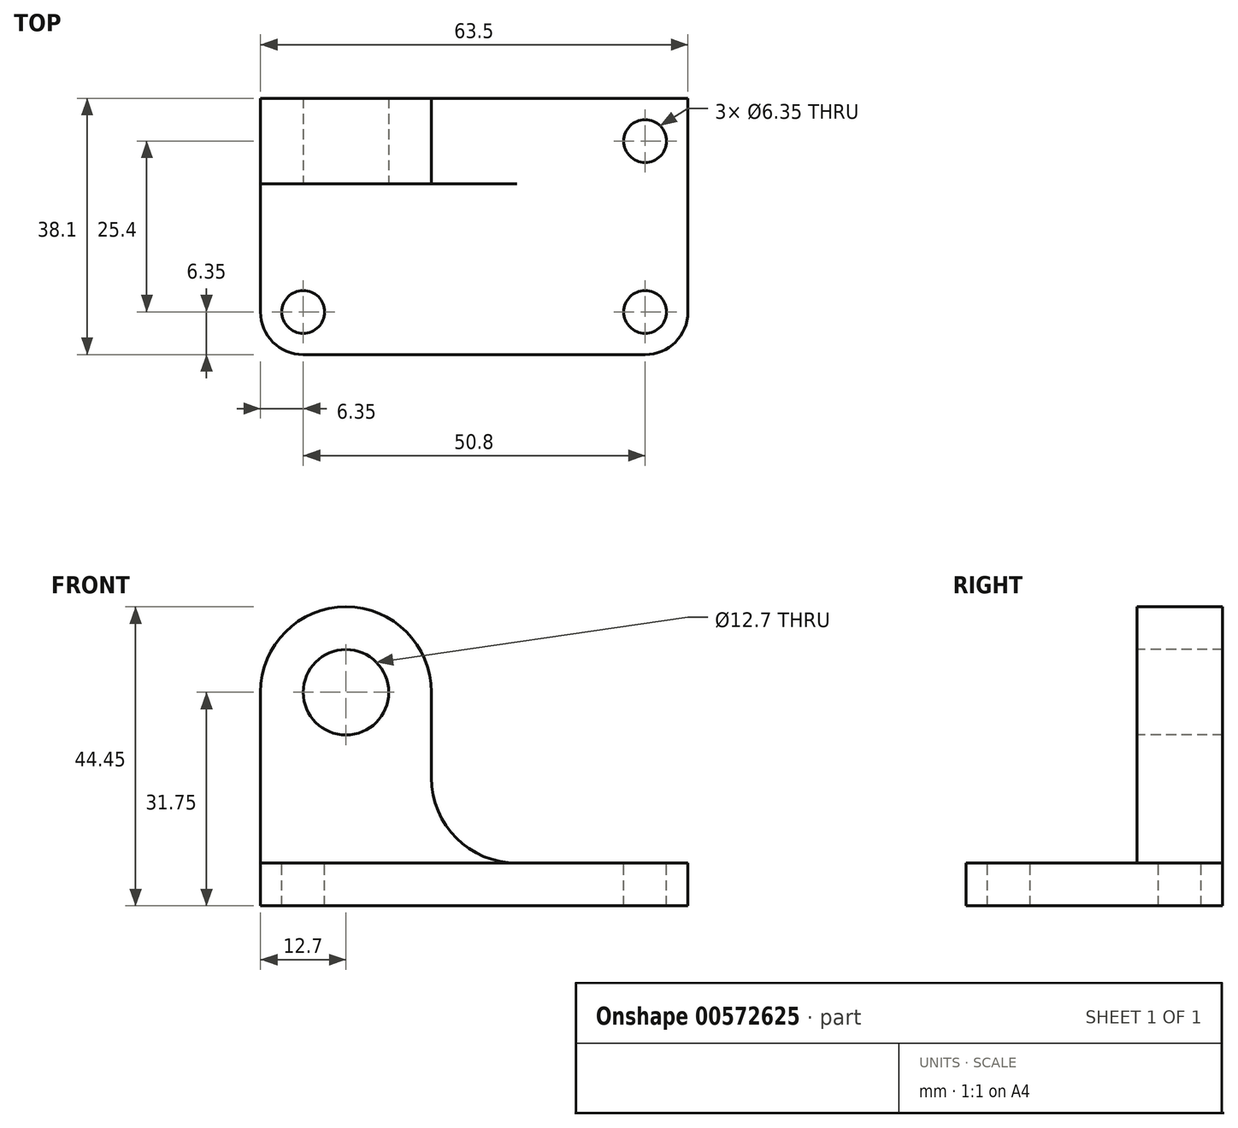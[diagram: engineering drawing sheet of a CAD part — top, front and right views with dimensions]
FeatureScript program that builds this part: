
annotation { "Feature Type Name" : "Feature", "Feature Type Description" : "" }
export const myFeature = defineFeature(function(context is Context, id is Id, definition is map)
    precondition{}
    {
        {
            var Q0;
            Q0=qCreatedBy(makeId("Front.planeOp"),FACE);
            var sketch = newSketch(context, id + "F0", { "sketchPlane" : qUnion([Q0])});
            skLineSegment(sketch, "E0", {"start": v(0, 0) * mm, "end": v(63.5, 0) * mm});
            skLineSegment(sketch, "E1", {"start": v(63.5, 0) * mm, "end": v(63.5, 6.35) * mm});
            skLineSegment(sketch, "E2", {"start": v(63.5, 6.35) * mm, "end": v(38.1, 6.35) * mm});
            skLineSegment(sketch, "E3", {"start": v(38.1, 6.35) * mm, "end": v(38.1, 44.45) * mm});
            skLineSegment(sketch, "E4", {"start": v(38.1, 44.45) * mm, "end": v(0, 44.45) * mm});
            skLineSegment(sketch, "E5", {"start": v(0, 44.45) * mm, "end": v(0, 0) * mm});
            skSolve(sketch);
        }
        {
            var Q0;
            Q0 = qSketchRegion(id + "F0", true);
            extrude(context, id + "F1", {"entities" : qUnion([Q0]), "depth" : 38.1 * mm, "offsetDistance" : 25.4 * mm});
        }
        {
            var Q0;
            Q0=makeQuery(id+"F1.opExtrude","SWEPT_FACE",FACE,{"disambiguationData":[OSD([sQuery(id+"F0.wireOp",EDGE,"E3")])]});
            var sketch = newSketch(context, id + "F2", { "sketchPlane" : qUnion([Q0])});
            skLineSegment(sketch, "E6", {"start": v(-38.1, 6.35) * mm, "end": v(-12.7, 6.35) * mm});
            skLineSegment(sketch, "E7", {"start": v(-12.7, 6.35) * mm, "end": v(-12.7, 44.45) * mm});
            skSolve(sketch);
        }
        {
            var Q0;
            Q0 = qSketchRegion(id + "F2", true);
            var Q1;
            Q1=makeQuery(id+"F2.imprint","IMPRINT",FACE,{"disambiguationData":[TD([[makeQuery(id+"F2.imprint","IMPRINT",EDGE,{"derivedFrom":sQuery(id+"F2.wireOp",EDGE,"E6")}),1.0]])]});
            extrude(context, id + "F3", {"entities" : qUnion([Q0, Q1]), "operationType" : NewBodyOperationType.REMOVE, "oppositeDirection" : true, "depth" : 38.1 * mm, "offsetDistance" : 25.4 * mm});
        }
        {
            var Q0;
            Q0=makeQuery(id+"F3.boolean.opBoolean","COPY",FACE,{"derivedFrom":makeQuery(id+"F3.opExtrude","SWEPT_FACE",FACE,{"disambiguationData":[OSD([sQuery(id+"F2.wireOp",EDGE,"E7")])]})});
            var sketch = newSketch(context, id + "F4", { "sketchPlane" : qUnion([Q0])});
            skLineSegment(sketch, "E8", {"start": v(25.4, 31.75) * mm, "end": v(25.4, 19.05) * mm});
            skArc(sketch, "E9", {"start": v(25.4, 19.05) * mm, "mid": v(29.12, 10.07) * mm, "end": v(38.1, 6.35) * mm});
            skArc(sketch, "E10", {"start": v(25.4, 31.75) * mm, "mid": v(21.68, 40.73) * mm, "end": v(12.7, 44.45) * mm});
            skArc(sketch, "E11", {"start": v(12.7, 44.45) * mm, "mid": v(3.72, 40.73) * mm, "end": v(0, 31.75) * mm});
            skCircle(sketch, "E12", {"center": v(12.7, 31.75) * mm, "radius": 6.35 * mm});
            skSolve(sketch);
        }
        {
            var Q0;
            Q0 = qSketchRegion(id + "F4", true);
            var Q1;
            Q1=makeQuery(id+"F4.imprint","IMPRINT",FACE,{"disambiguationData":[TD([[makeQuery(id+"F4.imprint","IMPRINT",EDGE,{"derivedFrom":sQuery(id+"F4.wireOp",EDGE,"E8")}),1.0]])]});
            var Q2;
            {var subQ0=sQuery(id+"F4.wireOp",EDGE,"E11");Q2=makeQuery(id+"F4.imprint","IMPRINT",FACE,{"disambiguationData":[TD([[makeQuery(id+"F4.imprint","IMPRINT",EDGE,{"derivedFrom":subQ0}),-1.0]])]});}
            extrude(context, id + "F5", {"entities" : qUnion([Q0, Q1, Q2]), "operationType" : NewBodyOperationType.REMOVE, "oppositeDirection" : true, "depth" : 12.7 * mm, "offsetDistance" : 25.4 * mm});
        }
        {
            var Q0;
            Q0=makeQuery(id+"F3.boolean.opBoolean","MERGE",FACE,{"derivedFrom":[makeQuery(id+"F1.opExtrude","SWEPT_FACE",FACE,{"disambiguationData":[OSD([sQuery(id+"F0.wireOp",EDGE,"E2")])]}),makeQuery(id+"F3.opExtrude","SWEPT_FACE",FACE,{"disambiguationData":[OSD([sQuery(id+"F2.wireOp",EDGE,"E6")])]})]});
            var sketch = newSketch(context, id + "F6", { "sketchPlane" : qUnion([Q0])});
            skArc(sketch, "E13", {"start": v(0, -31.75) * mm, "mid": v(1.86, -36.24) * mm, "end": v(6.35, -38.1) * mm});
            skArc(sketch, "E14", {"start": v(57.15, -38.1) * mm, "mid": v(61.64, -36.24) * mm, "end": v(63.5, -31.75) * mm});
            skCircle(sketch, "E15", {"center": v(6.35, -31.75) * mm, "radius": 3.18 * mm});
            skCircle(sketch, "E16", {"center": v(57.15, -31.75) * mm, "radius": 3.18 * mm});
            skCircle(sketch, "E17", {"center": v(57.15, -6.35) * mm, "radius": 3.18 * mm});
            skSolve(sketch);
        }
        {
            var Q0;
            Q0=makeQuery(id+"F6.imprint","IMPRINT",FACE,{"disambiguationData":[TD([[makeQuery(id+"F6.imprint","IMPRINT",EDGE,{"derivedFrom":sQuery(id+"F6.wireOp",EDGE,"E16")}),1.0]])]});
            var Q1;
            Q1=makeQuery(id+"F6.imprint","IMPRINT",FACE,{"disambiguationData":[TD([[makeQuery(id+"F6.imprint","IMPRINT",EDGE,{"derivedFrom":sQuery(id+"F6.wireOp",EDGE,"E17")}),1.0]])]});
            var Q2;
            Q2=makeQuery(id+"F6.imprint","IMPRINT",FACE,{"disambiguationData":[TD([[makeQuery(id+"F6.imprint","IMPRINT",EDGE,{"derivedFrom":sQuery(id+"F6.wireOp",EDGE,"E15")}),1.0]])]});
            var Q3;
            {var subQ0=sQuery(id+"F6.wireOp",EDGE,"E13");Q3=makeQuery(id+"F6.imprint","IMPRINT",FACE,{"disambiguationData":[TD([[makeQuery(id+"F6.imprint","IMPRINT",EDGE,{"derivedFrom":subQ0}),-1.0]])]});}
            var Q4;
            {var subQ0=sQuery(id+"F6.wireOp",EDGE,"E14");Q4=makeQuery(id+"F6.imprint","IMPRINT",FACE,{"disambiguationData":[TD([[makeQuery(id+"F6.imprint","IMPRINT",EDGE,{"derivedFrom":subQ0}),-1.0]])]});}
            var Q5;
            {var subQ0=sQuery(id+"F6.wireOp",EDGE,"E13");Q5=makeQuery(id+"F6.imprint","IMPRINT",FACE,{"disambiguationData":[TD([[makeQuery(id+"F6.imprint","IMPRINT",EDGE,{"derivedFrom":subQ0}),-1.0]])]});}
            var Q6;
            {var subQ0=sQuery(id+"F6.wireOp",EDGE,"E14");Q6=makeQuery(id+"F6.imprint","IMPRINT",FACE,{"disambiguationData":[TD([[makeQuery(id+"F6.imprint","IMPRINT",EDGE,{"derivedFrom":subQ0}),-1.0]])]});}
            extrude(context, id + "F7", {"entities" : qUnion([Q0, Q1, Q2, Q3, Q4, Q5, Q6]), "operationType" : NewBodyOperationType.REMOVE, "oppositeDirection" : true, "depth" : 6.35 * mm, "offsetDistance" : 25.4 * mm});
        }
    });
